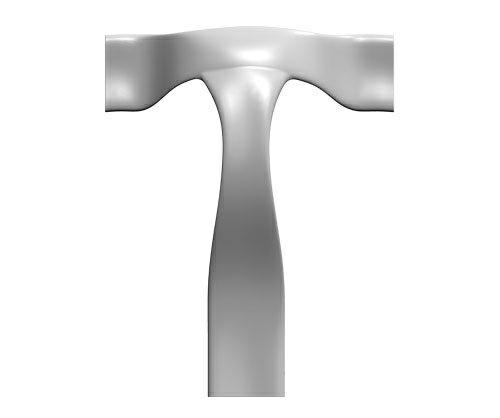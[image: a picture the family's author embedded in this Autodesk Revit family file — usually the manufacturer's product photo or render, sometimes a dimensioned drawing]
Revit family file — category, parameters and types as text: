
# Revit family: CITY ALPHABET litera „T”
name_source: partatom
category: Meble
revit_build: Autodesk Revit 2018 (Build: 20190510_1515(x64)
units: mm (PartAtom-declared; Revit-internal decimal feet)

## family parameters
Numer OmniClass = 23.40.10.11.14
Obiekt nadrzędny = Powierzchnia
Punkt obliczania pomieszczeń = Nie
Tnij formami wycięć po wczytaniu = Nie
Tytuł OmniClass = Exterior Seating
Współdzielony = Nie

## types (1)
- CITY ALPHABET litera „T”
    Domyślna rzędna = 1219 mm
    Długość = 2310 mm  [stored 7.57874 ft]
    IfcExportAs = IfcFurnishingElement
    Komentarze do typu = Ławka
    Materiał - informacja = Szeroki wybór kolorów wg palety RAL. Istnieje również możliwość specjalnego wykonania
kolorystycznego na indywidualne zapytanie klienta.
    Model = CITY ALPHABET litera „T”
    Obraz typu = T.jpg
    Producent = Astrini Design
    Szerokość = 1800 mm  [stored 5.90551 ft]
    Temepratura użytkowania = -40°C do 80°C, ( -40°F do 176°F )
    URL = http://astrini-design.pl
    Waga (szacunkowo) = 41.00 kg
    Waga po wypełnieniu (szacunkowo) = 91.00 kg
    Wysokość = 710 mm

note: [stored X ft] marks values corroborated as IEEE doubles in the binary element streams (Revit-internal decimal feet)
